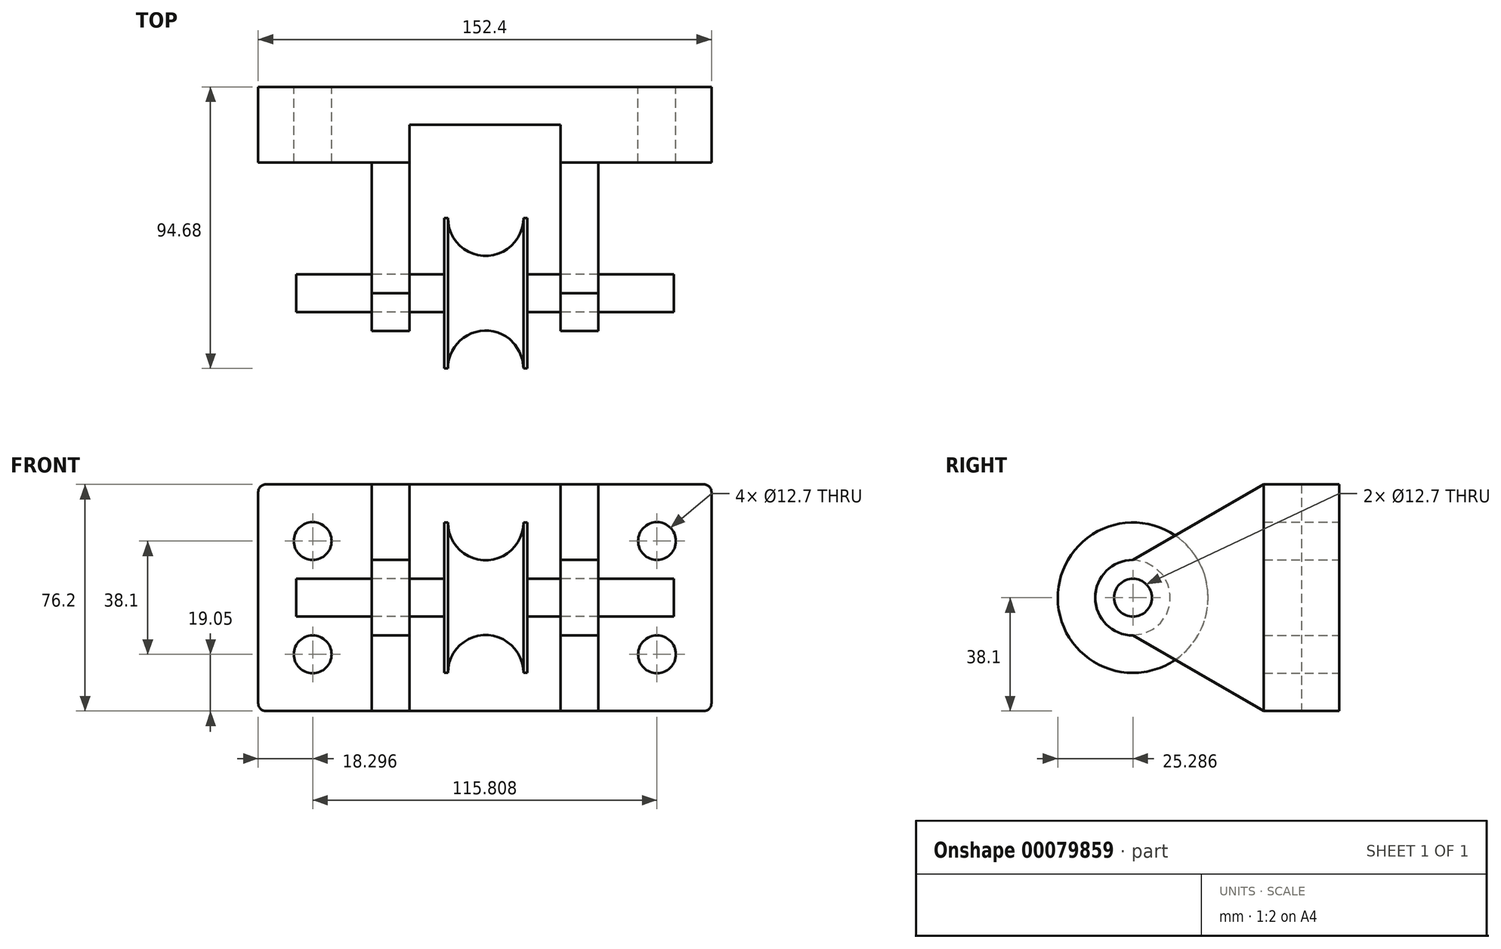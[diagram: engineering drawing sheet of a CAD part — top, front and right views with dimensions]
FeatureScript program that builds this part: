
annotation { "Feature Type Name" : "Feature", "Feature Type Description" : "" }
export const myFeature = defineFeature(function(context is Context, id is Id, definition is map)
    precondition{}
    {
        {
            var Q0;
            Q0=qCreatedBy(makeId("Front.planeOp"),FACE);
            var sketch = newSketch(context, id + "F0", { "sketchPlane" : qUnion([Q0])});
            skLineSegment(sketch, "E0.bottom", {"start": v(-76.2, 38.1) * mm, "end": v(76.2, 38.1) * mm});
            skLineSegment(sketch, "E0.top", {"start": v(-76.2, -38.1) * mm, "end": v(76.2, -38.1) * mm});
            skLineSegment(sketch, "E0.left", {"start": v(-76.2, 38.1) * mm, "end": v(-76.2, -38.1) * mm});
            skLineSegment(sketch, "E0.right", {"start": v(76.2, 38.1) * mm, "end": v(76.2, -38.1) * mm});
            skLineSegment(sketch, "E1.bottom", {"start": v(0, 38.1) * mm, "end": v(0, 38.1) * mm});
            skLineSegment(sketch, "E1.top", {"start": v(0, -38.1) * mm, "end": v(0, -38.1) * mm});
            skLineSegment(sketch, "E1.left", {"start": v(0, 38.1) * mm, "end": v(0, -38.1) * mm, "construction": true});
            skLineSegment(sketch, "E1.right", {"start": v(0, 38.1) * mm, "end": v(0, -38.1) * mm, "construction": true});
            skLineSegment(sketch, "E2.bottom", {"start": v(-76.2, 0) * mm, "end": v(76.2, 0) * mm, "construction": true});
            skLineSegment(sketch, "E2.top", {"start": v(-76.2, 0) * mm, "end": v(76.2, 0) * mm, "construction": true});
            skLineSegment(sketch, "E2.left", {"start": v(-76.2, 0) * mm, "end": v(-76.2, 0) * mm});
            skLineSegment(sketch, "E2.right", {"start": v(76.2, 0) * mm, "end": v(76.2, 0) * mm});
            skCircle(sketch, "E3", {"center": v(-57.9, 19.05) * mm, "radius": 6.35 * mm});
            skCircle(sketch, "E4.MirrorC", {"center": v(-57.9, -19.05) * mm, "radius": 6.35 * mm});
            skLineSegment(sketch, "E5.MirrorCS", {"start": v(0, -38.1) * mm, "end": v(0, 38.1) * mm, "construction": true});
            skCircle(sketch, "E6.MirrorC", {"center": v(57.9, 19.05) * mm, "radius": 6.35 * mm});
            skCircle(sketch, "E7.MirrorC", {"center": v(57.9, -19.05) * mm, "radius": 6.35 * mm});
            skSolve(sketch);
        }
        {
            var Q0;
            Q0=makeQuery(id+"F0.imprint","IMPRINT",FACE,{"disambiguationData":[TD([[makeQuery(id+"F0.imprint","IMPRINT",EDGE,{"derivedFrom":sQuery(id+"F0.wireOp",EDGE,"E0.bottom")}),-1.0]])]});
            extrude(context, id + "F1", {"entities" : qUnion([Q0]), "depth" : 12.7 * mm});
        }
        {
            var Q0;
            Q0=makeQuery(id+"F1.opExtrude","SWEPT_EDGE",EDGE,{"disambiguationData":[OSD([sQuery(id+"F0.wireOp",EDGE,"E0.bottom"),sQuery(id+"F0.wireOp",EDGE,"E0.left")])]});
            var Q1;
            Q1=makeQuery(id+"F1.opExtrude","SWEPT_EDGE",EDGE,{"disambiguationData":[OSD([sQuery(id+"F0.wireOp",EDGE,"E0.bottom"),sQuery(id+"F0.wireOp",EDGE,"E0.right")])]});
            var Q2;
            Q2=makeQuery(id+"F1.opExtrude","SWEPT_EDGE",EDGE,{"disambiguationData":[OSD([sQuery(id+"F0.wireOp",EDGE,"E0.top"),sQuery(id+"F0.wireOp",EDGE,"E0.left")])]});
            var Q3;
            Q3=makeQuery(id+"F1.opExtrude","SWEPT_EDGE",EDGE,{"disambiguationData":[OSD([sQuery(id+"F0.wireOp",EDGE,"E0.top"),sQuery(id+"F0.wireOp",EDGE,"E0.right")])]});
            fillet(context, id + "F2", {"entities" : qUnion([Q0, Q1, Q2, Q3]), "radius" : 2.54 * mm, "tangentPropagation" : true, "allowEdgeOverflow" : false});
        }
        {
            var Q0;
            Q0=makeQuery(id+"F1.opExtrude","CAP_FACE",FACE,{"disambiguationData":[OSD([sQuery(id+"F0.wireOp",EDGE,"E0.bottom"),sQuery(id+"F0.wireOp",EDGE,"E0.top"),sQuery(id+"F0.wireOp",EDGE,"E0.left"),sQuery(id+"F0.wireOp",EDGE,"E0.right"),sQuery(id+"F0.wireOp",EDGE,"E3"),sQuery(id+"F0.wireOp",EDGE,"E4.MirrorC"),sQuery(id+"F0.wireOp",EDGE,"E6.MirrorC"),sQuery(id+"F0.wireOp",EDGE,"E7.MirrorC")])],"isStart":false});
            var sketch = newSketch(context, id + "F3", { "sketchPlane" : qUnion([Q0])});
            skLineSegment(sketch, "E8.0.0", {"start": v(73.66, 38.1) * mm, "end": v(-73.66, 38.1) * mm});
            skArc(sketch, "E8.0.1", {"start": v(-73.66, 38.1) * mm, "mid": v(-75.46, 37.36) * mm, "end": v(-76.2, 35.56) * mm});
            skLineSegment(sketch, "E8.0.2", {"start": v(-76.2, 35.56) * mm, "end": v(-76.2, -35.56) * mm});
            skArc(sketch, "E8.0.3", {"start": v(-76.2, -35.56) * mm, "mid": v(-75.46, -37.36) * mm, "end": v(-73.66, -38.1) * mm});
            skLineSegment(sketch, "E8.0.4", {"start": v(-73.66, -38.1) * mm, "end": v(73.66, -38.1) * mm});
            skArc(sketch, "E8.0.5", {"start": v(73.66, -38.1) * mm, "mid": v(75.46, -37.36) * mm, "end": v(76.2, -35.56) * mm});
            skLineSegment(sketch, "E8.0.6", {"start": v(76.2, -35.56) * mm, "end": v(76.2, 35.56) * mm});
            skArc(sketch, "E8.0.7", {"start": v(76.2, 35.56) * mm, "mid": v(75.46, 37.36) * mm, "end": v(73.66, 38.1) * mm});
            skLineSegment(sketch, "E9", {"start": v(-38.1, 38.1) * mm, "end": v(-38.1, -38.1) * mm});
            skSolve(sketch);
        }
        {
            var Q0;
            {var subQ1=sQuery(id+"F3.wireOp",EDGE,"E8.0.1");Q0=makeQuery(id+"F3.imprint","IMPRINT",FACE,{"disambiguationData":[TD([[makeQuery(id+"F3.imprint","IMPRINT",EDGE,{"derivedFrom":subQ1}),1.0]])]});}
            extrude(context, id + "F4", {"entities" : qUnion([Q0]), "depth" : 12.7 * mm});
        }
        {
            var Q0;
            Q0=makeQuery(id+"F4.opExtrude","SWEPT_FACE",FACE,{"disambiguationData":[OSD([sQuery(id+"F3.wireOp",EDGE,"E9")])]});
            var sketch = newSketch(context, id + "F5", { "sketchPlane" : qUnion([Q0])});
            skLineSegment(sketch, "E10", {"start": v(-25.4, -38.1) * mm, "end": v(-69.4, -12.7) * mm});
            skLineSegment(sketch, "E11", {"start": v(-25.4, 38.1) * mm, "end": v(-69.4, 12.7) * mm});
            skLineSegment(sketch, "E12", {"start": v(-69.4, -12.7) * mm, "end": v(-69.4, 12.7) * mm});
            skCircle(sketch, "E13", {"center": v(-69.4, 0) * mm, "radius": 12.7 * mm});
            skCircle(sketch, "E14", {"center": v(-69.4, 0) * mm, "radius": 6.35 * mm});
            skLineSegment(sketch, "E15.0.0", {"start": v(-12.7, -38.1) * mm, "end": v(-12.7, 38.1) * mm});
            skLineSegment(sketch, "E15.0.1", {"start": v(-12.7, 38.1) * mm, "end": v(-25.4, 38.1) * mm});
            skLineSegment(sketch, "E15.0.2", {"start": v(-25.4, 38.1) * mm, "end": v(-25.4, -38.1) * mm});
            skLineSegment(sketch, "E15.0.3", {"start": v(-25.4, -38.1) * mm, "end": v(-12.7, -38.1) * mm});
            skSolve(sketch);
        }
        {
            var Q0;
            {var subQ0=sQuery(id+"F5.wireOp",EDGE,"E10");Q0=makeQuery(id+"F5.imprint","IMPRINT",FACE,{"disambiguationData":[TD([[makeQuery(id+"F5.imprint","IMPRINT",EDGE,{"derivedFrom":subQ0}),-1.0]])]});}
            var Q1;
            Q1=makeQuery(id+"F5.imprint","IMPRINT",FACE,{"disambiguationData":[TD([[makeQuery(id+"F5.imprint","IMPRINT",EDGE,{"derivedFrom":sQuery(id+"F5.wireOp",EDGE,"E15.0.0")}),-1.0]])]});
            var Q2;
            {var subQ1=sQuery(id+"F5.wireOp",EDGE,"E12");var subQ3=sQuery(id+"F5.wireOp",EDGE,"E14");var subQ4=makeQuery(id+"F5.imprint","INTERSECT",VERTEX,{"disambiguationData":[OD(0.0)],"derivedFrom":[subQ1,subQ3]});Q2=makeQuery(id+"F5.imprint","IMPRINT",FACE,{"disambiguationData":[TD([[makeQuery(id+"F5.imprint","IMPRINT",EDGE,{"disambiguationData":[TD([[subQ4,1.0]])],"derivedFrom":subQ3}),-1.0]])]});}
            var Q3;
            {var subQ1=sQuery(id+"F5.wireOp",EDGE,"E12");var subQ3=sQuery(id+"F5.wireOp",EDGE,"E14");var subQ4=makeQuery(id+"F5.imprint","INTERSECT",VERTEX,{"disambiguationData":[OD(0.0)],"derivedFrom":[subQ1,subQ3]});Q3=makeQuery(id+"F5.imprint","IMPRINT",FACE,{"disambiguationData":[TD([[makeQuery(id+"F5.imprint","IMPRINT",EDGE,{"disambiguationData":[TD([[subQ4,-1.0]])],"derivedFrom":subQ3}),-1.0]])]});}
            extrude(context, id + "F6", {"entities" : qUnion([Q0, Q1, Q2, Q3]), "operationType" : NewBodyOperationType.ADD, "depth" : 12.7 * mm});
        }
        {
            var Q0;
            Q0=makeQuery(id+"F1.opExtrude","SWEPT_BODY",BODY,{"disambiguationData":[OSD([sQuery(id+"F0.wireOp",EDGE,"E0.bottom"),sQuery(id+"F0.wireOp",EDGE,"E0.top"),sQuery(id+"F0.wireOp",EDGE,"E0.left"),sQuery(id+"F0.wireOp",EDGE,"E0.right"),sQuery(id+"F0.wireOp",EDGE,"E3"),sQuery(id+"F0.wireOp",EDGE,"E4.MirrorC"),sQuery(id+"F0.wireOp",EDGE,"E6.MirrorC"),sQuery(id+"F0.wireOp",EDGE,"E7.MirrorC")])]});
            var Q1;
            Q1=qCreatedBy(makeId("Right.planeOp"),FACE);
            mirror(context, id + "F7", {"operationType" : NewBodyOperationType.ADD, "entities" : qUnion([Q0]), "mirrorPlane" : qUnion([Q1])});
        }
        {
            var Q0;
            Q0=makeQuery(id+"F7.opPattern","COPY",FACE,{"derivedFrom":makeQuery(id+"F6.opExtrude","CAP_FACE",FACE,{"disambiguationData":[OSD([sQuery(id+"F5.wireOp",EDGE,"E10"),sQuery(id+"F5.wireOp",EDGE,"E11"),sQuery(id+"F5.wireOp",EDGE,"E13"),sQuery(id+"F5.wireOp",EDGE,"E14"),sQuery(id+"F5.wireOp",EDGE,"E15.0.0"),sQuery(id+"F5.wireOp",EDGE,"E15.0.1"),sQuery(id+"F5.wireOp",EDGE,"E15.0.3")])],"isStart":true}),"instanceName":"1"});
            var sketch = newSketch(context, id + "F8", { "sketchPlane" : qUnion([Q0])});
            skCircle(sketch, "E16.0", {"center": v(-69.4, 0) * mm, "radius": 6.35 * mm});
            skSolve(sketch);
        }
        {
            var Q0;
            Q0=makeQuery(id+"F8.imprint","IMPRINT",FACE,{"disambiguationData":[TD([[makeQuery(id+"F8.imprint","IMPRINT",EDGE,{"derivedFrom":sQuery(id+"F8.wireOp",EDGE,"E16.0")}),1.0]])]});
            extrude(context, id + "F9", {"entities" : qUnion([Q0]), "depth" : 25.4 * mm, "hasSecondDirection" : true, "secondDirectionOppositeDirection" : true, "secondDirectionDepth" : 101.6 * mm});
        }
        {
            var Q0;
            Q0=qCreatedBy(makeId("Top.planeOp"),FACE);
            var sketch = newSketch(context, id + "F10", { "sketchPlane" : qUnion([Q0])});
            skLineSegment(sketch, "E17.bottom", {"start": v(-13.7, -75.74) * mm, "end": v(14.24, -75.74) * mm, "construction": true});
            skLineSegment(sketch, "E17.top", {"start": v(-13.7, -94.68) * mm, "end": v(-12.43, -94.68) * mm});
            skLineSegment(sketch, "E17.left", {"start": v(-13.7, -75.74) * mm, "end": v(-13.7, -94.68) * mm});
            skLineSegment(sketch, "E17.right", {"start": v(14.24, -75.74) * mm, "end": v(14.24, -94.68) * mm});
            skLineSegment(sketch, "E18", {"start": v(-63.5, -63.04) * mm, "end": v(63.5, -63.04) * mm, "construction": true});
            skLineSegment(sketch, "E19", {"start": v(63.5, -75.74) * mm, "end": v(-63.5, -75.74) * mm, "construction": true});
            skLineSegment(sketch, "E20", {"start": v(0.27, -94.68) * mm, "end": v(0.27, -75.74) * mm, "construction": true});
            skArc(sketch, "E21", {"start": v(12.97, -94.68) * mm, "mid": v(0.27, -81.98) * mm, "end": v(-12.43, -94.68) * mm});
            skLineSegment(sketch, "E22.trimOffspring", {"start": v(12.97, -94.68) * mm, "end": v(14.24, -94.68) * mm});
            skLineSegment(sketch, "E23", {"start": v(-13.7, -75.74) * mm, "end": v(14.24, -75.74) * mm});
            skSolve(sketch);
        }
        {
            var Q0;
            Q0=makeQuery(id+"F10.imprint","IMPRINT",FACE,{"disambiguationData":[TD([[makeQuery(id+"F10.imprint","IMPRINT",EDGE,{"derivedFrom":sQuery(id+"F10.wireOp",EDGE,"E17.top")}),1.0]])]});
            var Q1;
            Q1=makeQuery(id+"F9.opExtrude","SWEPT_FACE",FACE,{"disambiguationData":[OSD([sQuery(id+"F8.wireOp",EDGE,"E16.0")])]});
            revolve(context, id + "F11", {"operationType" : NewBodyOperationType.ADD, "entities" : qUnion([Q0]), "axis" : qUnion([Q1]), "revolveType" : RevolveType.FULL});
        }
    });
